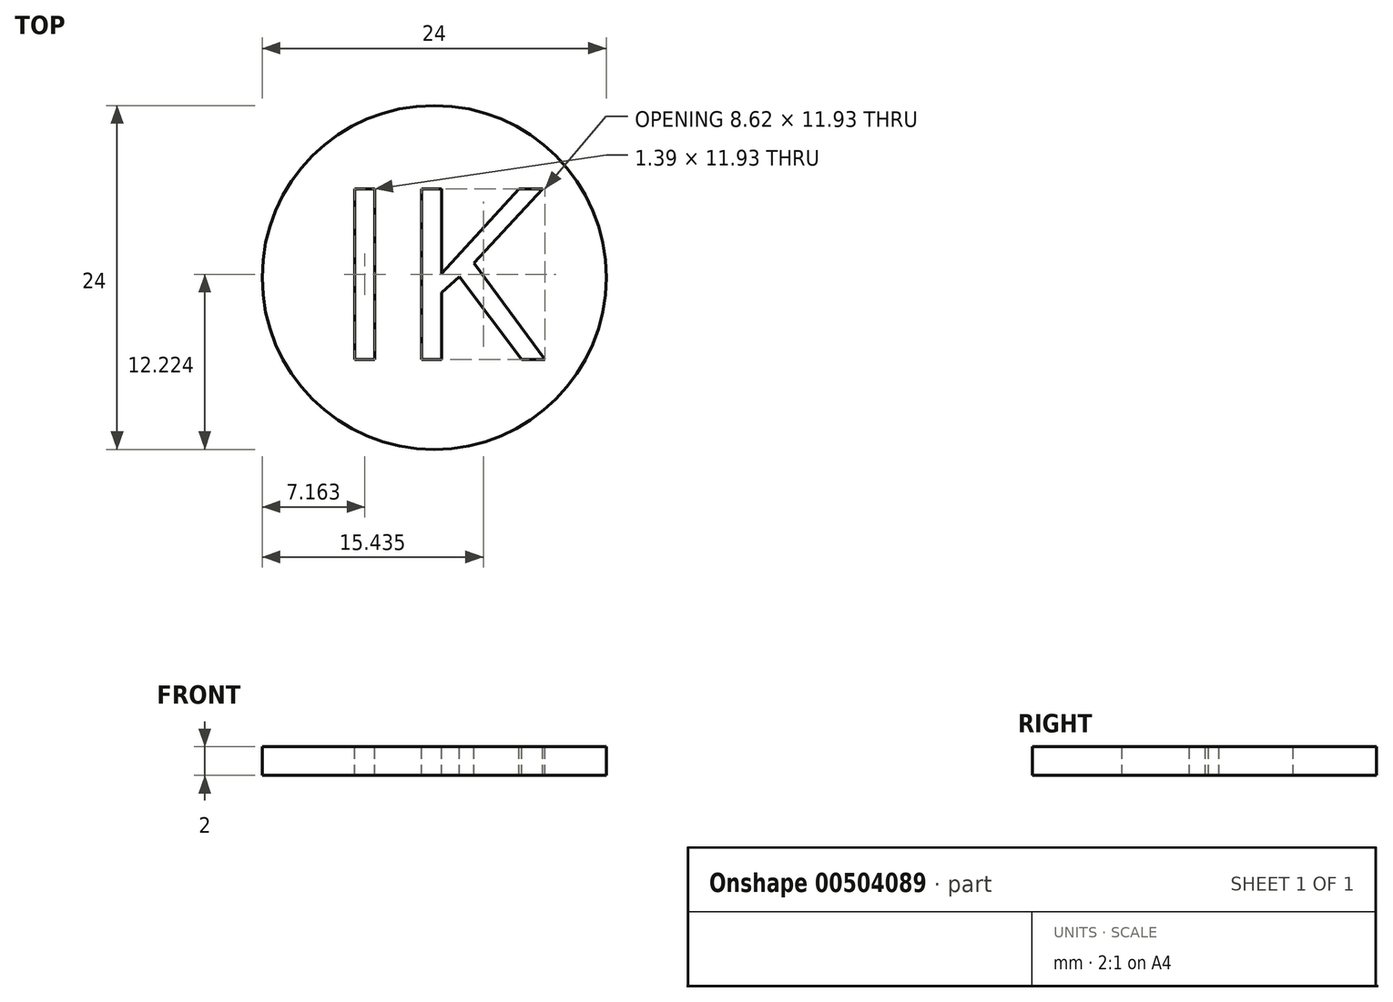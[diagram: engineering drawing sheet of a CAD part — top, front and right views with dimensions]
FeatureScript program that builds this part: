
annotation { "Feature Type Name" : "Feature", "Feature Type Description" : "" }
export const myFeature = defineFeature(function(context is Context, id is Id, definition is map)
    precondition{}
    {
        {
            var Q0;
            Q0=qCreatedBy(makeId("Top.planeOp"),FACE);
            var sketch = newSketch(context, id + "F0", { "sketchPlane" : qUnion([Q0])});
            skCircle(sketch, "E0", {"center": v(0, 0) * mm, "radius": 12 * mm});
            skSolve(sketch);
        }
        {
            var Q0;
            Q0=qSketchRegion(id+"F0",true);
            extrude(context, id + "F1", {"entities" : qUnion([Q0]), "depth" : 2 * mm});
        }
        {
            var Q0;
            Q0=makeQuery(id+"F1.opExtrude","CAP_FACE",FACE,{"disambiguationData":[OSD([sQuery(id+"F0.wireOp",EDGE,"E0")])],"isStart":false});
            var sketch = newSketch(context, id + "F2", { "sketchPlane" : qUnion([Q0])});
            skText(sketch, "E1", { "text": "IK", "fontName": "OpenSans-Regular.ttf"});
            const initialGuessF2  = {"E1": [-0.00717, -0.00574, 1, 0, 0.01203]};
            skSetInitialGuess(sketch, initialGuessF2);
            skSolve(sketch);
        }
        {
            var Q0;
            Q0 = qSketchRegion(id + "F2", true);
            extrude(context, id + "F3", {"entities" : qUnion([Q0]), "operationType" : NewBodyOperationType.REMOVE, "oppositeDirection" : true, "depth" : 25 * mm});
        }
    });
